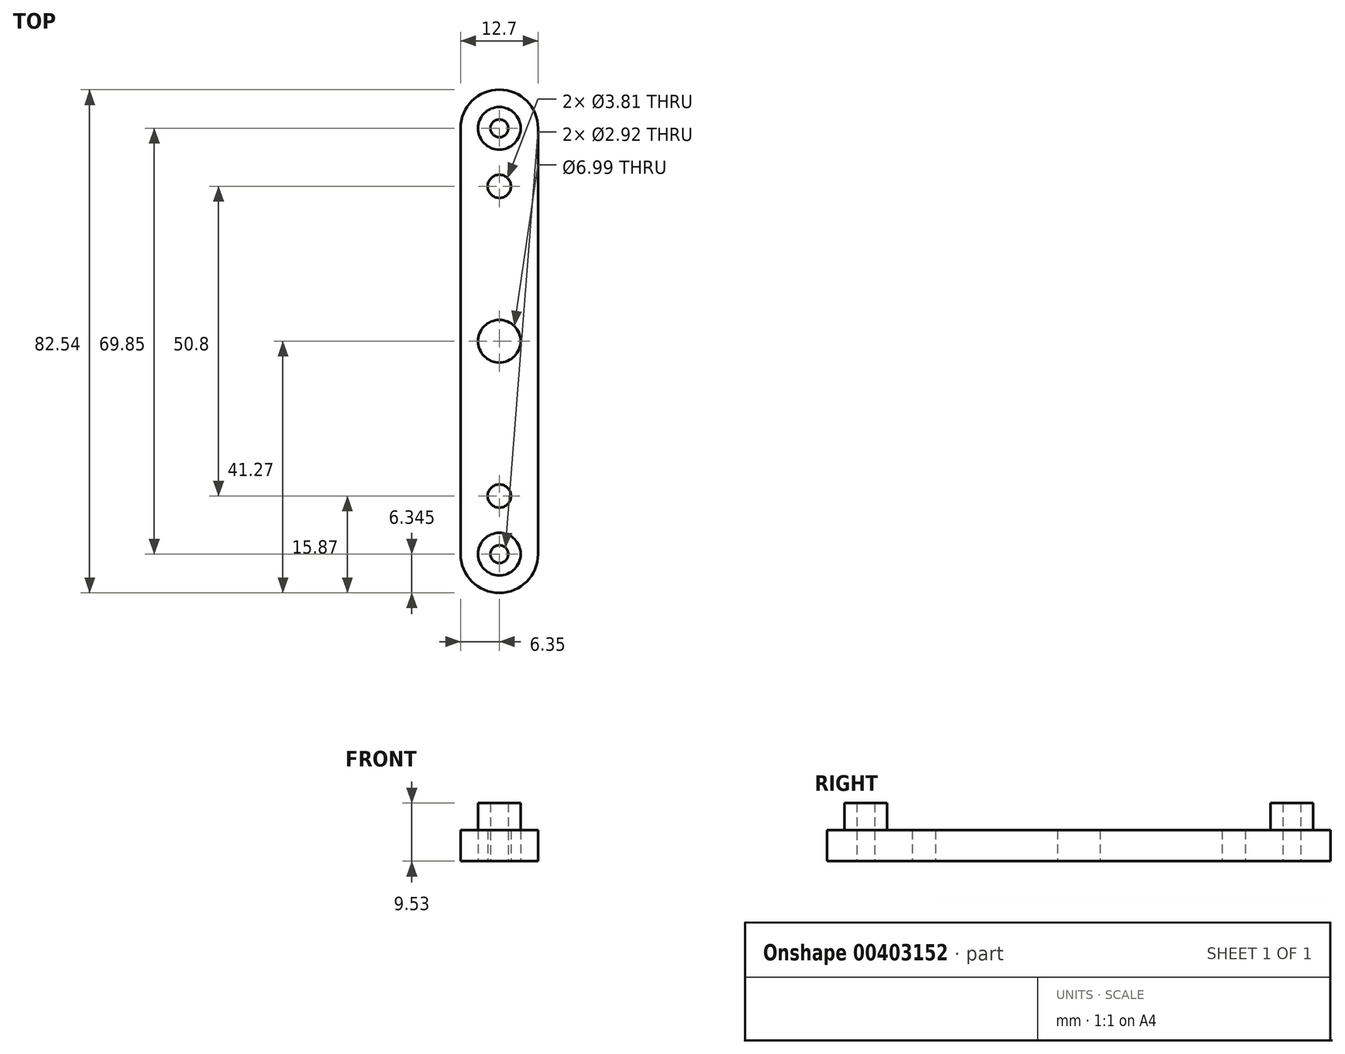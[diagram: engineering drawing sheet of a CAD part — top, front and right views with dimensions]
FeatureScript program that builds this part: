
annotation { "Feature Type Name" : "Feature", "Feature Type Description" : "" }
export const myFeature = defineFeature(function(context is Context, id is Id, definition is map)
    precondition{}
    {
        {
            var Q0;
            Q0=qCreatedBy(makeId("Top.planeOp"),FACE);
            var sketch = newSketch(context, id + "F0", { "sketchPlane" : qUnion([Q0])});
            skLineSegment(sketch, "E0.bottom", {"start": v(0, -41.28) * mm, "end": v(0, -41.28) * mm});
            skLineSegment(sketch, "E0.top", {"start": v(0, 41.28) * mm, "end": v(0, 41.28) * mm});
            skLineSegment(sketch, "E0.left", {"start": v(6.35, -34.93) * mm, "end": v(6.35, 34.93) * mm});
            skLineSegment(sketch, "E0.right", {"start": v(-6.35, -34.93) * mm, "end": v(-6.35, 34.93) * mm});
            skPoint(sketch, "E0.middle", {"position": v(0, 0) * mm});
            skLineSegment(sketch, "E1", {"start": v(0, 34.93) * mm, "end": v(0, -34.93) * mm});
            skPoint(sketch, "E2", {"position": v(0, 25.4) * mm});
            skPoint(sketch, "E3", {"position": v(0, -25.4) * mm});
            skPoint(sketch, "E4.visualSharp", {"position": v(-6.35, 41.28) * mm});
            skArc(sketch, "E4.filletArc", {"start": v(0, 41.28) * mm, "mid": v(-4.5, 39.42) * mm, "end": v(-6.35, 34.93) * mm});
            skPoint(sketch, "E5.visualSharp", {"position": v(-6.35, -41.28) * mm});
            skArc(sketch, "E5.filletArc", {"start": v(-6.35, -34.93) * mm, "mid": v(-4.5, -39.42) * mm, "end": v(0, -41.27) * mm});
            skPoint(sketch, "E6.visualSharp", {"position": v(6.35, -41.28) * mm});
            skArc(sketch, "E6.filletArc", {"start": v(0, -41.27) * mm, "mid": v(4.5, -39.42) * mm, "end": v(6.35, -34.93) * mm});
            skPoint(sketch, "E7.visualSharp", {"position": v(6.35, 41.28) * mm});
            skArc(sketch, "E7.filletArc", {"start": v(6.35, 34.93) * mm, "mid": v(4.5, 39.42) * mm, "end": v(0, 41.27) * mm});
            skCircle(sketch, "E8", {"center": v(0, -25.4) * mm, "radius": 1.9 * mm});
            skCircle(sketch, "E9", {"center": v(0, 25.4) * mm, "radius": 1.9 * mm});
            skCircle(sketch, "E10", {"center": v(0, -34.93) * mm, "radius": 1.46 * mm});
            skCircle(sketch, "E11", {"center": v(0, 34.93) * mm, "radius": 1.46 * mm});
            skCircle(sketch, "E12", {"center": v(0, 0) * mm, "radius": 1.46 * mm});
            skCircle(sketch, "E13", {"center": v(0, 34.93) * mm, "radius": 3.5 * mm});
            skCircle(sketch, "E14", {"center": v(0, 0) * mm, "radius": 3.5 * mm});
            skCircle(sketch, "E15", {"center": v(0, -34.93) * mm, "radius": 3.5 * mm});
            skSolve(sketch);
        }
        {
            var Q0;
            Q0=makeQuery(id+"F0.imprint","IMPRINT",FACE,{"disambiguationData":[TD([[makeQuery(id+"F0.imprint","IMPRINT",EDGE,{"derivedFrom":sQuery(id+"F0.wireOp",EDGE,"E0.left")}),1.0]])]});
            extrude(context, id + "F1", {"entities" : qUnion([Q0]), "depth" : 5.08 * mm});
        }
        {
            var Q0;
            Q0=makeQuery(id+"F0.imprint","IMPRINT",FACE,{"disambiguationData":[TD([[makeQuery(id+"F0.imprint","IMPRINT",EDGE,{"derivedFrom":sQuery(id+"F0.wireOp",EDGE,"E10")}),-1.0]])]});
            var Q1;
            {var subQ0=sQuery(id+"F0.wireOp",EDGE,"E14");var subQ1=sQuery(id+"F0.wireOp",EDGE,"E1");var subQ2=makeQuery(id+"F0.imprint","INTERSECT",VERTEX,{"disambiguationData":[OD(0.0)],"derivedFrom":[subQ1,subQ0]});Q1=makeQuery(id+"F0.imprint","IMPRINT",FACE,{"disambiguationData":[TD([[makeQuery(id+"F0.imprint","IMPRINT",EDGE,{"disambiguationData":[TD([[subQ2,-1.0]])],"derivedFrom":subQ1}),1.0]])]});}
            var Q2;
            {var subQ0=sQuery(id+"F0.wireOp",EDGE,"E14");var subQ1=sQuery(id+"F0.wireOp",EDGE,"E1");var subQ2=makeQuery(id+"F0.imprint","INTERSECT",VERTEX,{"disambiguationData":[OD(0.0)],"derivedFrom":[subQ1,subQ0]});Q2=makeQuery(id+"F0.imprint","IMPRINT",FACE,{"disambiguationData":[TD([[makeQuery(id+"F0.imprint","IMPRINT",EDGE,{"disambiguationData":[TD([[subQ2,-1.0]])],"derivedFrom":subQ1}),-1.0]])]});}
            var Q3;
            Q3=makeQuery(id+"F0.imprint","IMPRINT",FACE,{"disambiguationData":[TD([[makeQuery(id+"F0.imprint","IMPRINT",EDGE,{"derivedFrom":sQuery(id+"F0.wireOp",EDGE,"E11")}),-1.0]])]});
            extrude(context, id + "F2", {"entities" : qUnion([Q0, Q1, Q2, Q3]), "operationType" : NewBodyOperationType.ADD, "depth" : 9.52 * mm});
        }
    });
